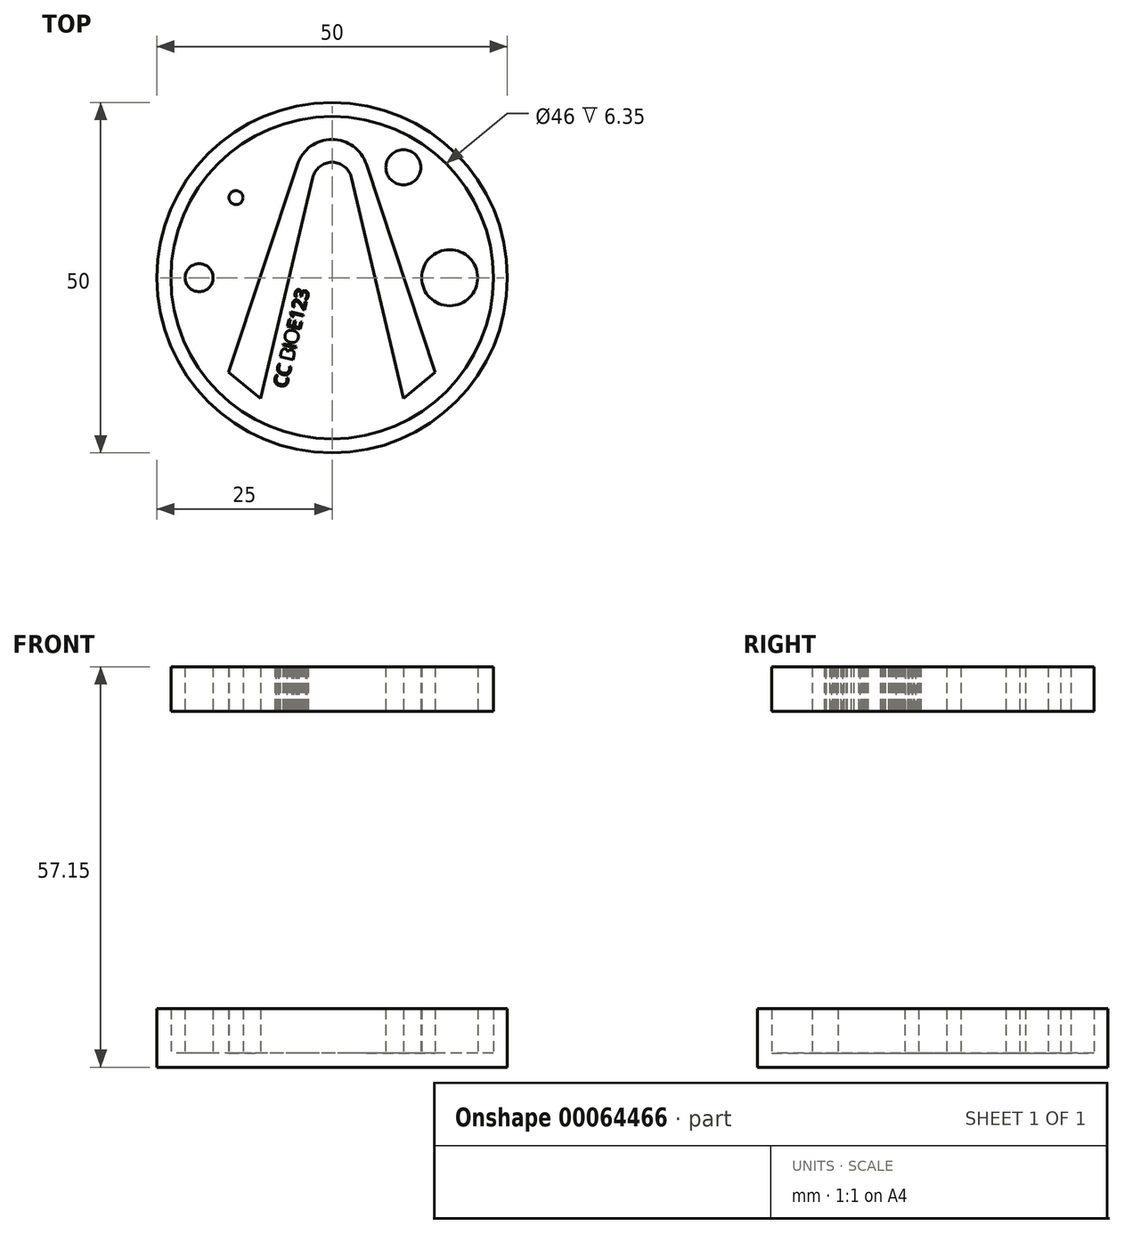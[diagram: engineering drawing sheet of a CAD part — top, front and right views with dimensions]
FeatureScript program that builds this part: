
annotation { "Feature Type Name" : "Feature", "Feature Type Description" : "" }
export const myFeature = defineFeature(function(context is Context, id is Id, definition is map)
    precondition{}
    {
        {
            var Q0;
            Q0=qCreatedBy(makeId("Top.planeOp"),FACE);
            var sketch = newSketch(context, id + "F0", { "sketchPlane" : qUnion([Q0])});
            skCircle(sketch, "E0", {"center": v(0, 0) * mm, "radius": 25 * mm});
            skCircle(sketch, "E1", {"center": v(0, 0) * mm, "radius": 23 * mm});
            skSolve(sketch);
        }
        {
            var Q0;
            Q0=makeQuery(id+"F0.imprint","IMPRINT",FACE,{"disambiguationData":[TD([[makeQuery(id+"F0.imprint","IMPRINT",EDGE,{"derivedFrom":sQuery(id+"F0.wireOp",EDGE,"E1")}),1.0]])]});
            extrude(context, id + "F1", {"entities" : qUnion([Q0]), "depth" : 2 * mm});
        }
        {
            var Q0;
            Q0=qCreatedBy(makeId("Top.planeOp"),FACE);
            cPlane(context, id + "F2", {"entities" : qUnion([Q0]), "cplaneType" : CPlaneType.OFFSET, "offset" : 50.8 * mm, "width" : 152.4 * mm, "height" : 152.4 * mm});
        }
        {
            var Q0;
            Q0=makeQuery(id+"F1.opExtrude","CAP_FACE",FACE,{"disambiguationData":[OSD([sQuery(id+"F0.wireOp",EDGE,"E1")])],"isStart":false});
            var sketch = newSketch(context, id + "F3", { "sketchPlane" : qUnion([Q0])});
            skArc(sketch, "E2", {"start": v(4.89, 16.16) * mm, "mid": v(-0.03, 19.72) * mm, "end": v(-4.95, 16.16) * mm});
            skArc(sketch, "E3", {"start": v(2.76, 14.29) * mm, "mid": v(0, 16.47) * mm, "end": v(-2.77, 14.29) * mm});
            skCircle(sketch, "E4", {"center": v(-18.97, 0) * mm, "radius": 2 * mm});
            skCircle(sketch, "E5", {"center": v(16.76, 0) * mm, "radius": 4 * mm});
            skCircle(sketch, "E6", {"center": v(-13.72, 11.43) * mm, "radius": 1 * mm});
            skCircle(sketch, "E7", {"center": v(10.16, 15.75) * mm, "radius": 2.5 * mm});
            skLineSegment(sketch, "E8", {"start": v(-4.95, 16.16) * mm, "end": v(-14.76, -13.5) * mm});
            skLineSegment(sketch, "E9", {"start": v(-2.77, 14.29) * mm, "end": v(-10.18, -17.21) * mm});
            skLineSegment(sketch, "E10", {"start": v(-14.76, -13.5) * mm, "end": v(-10.18, -17.21) * mm});
            skLineSegment(sketch, "E11", {"start": v(4.89, 16.16) * mm, "end": v(14.7, -13.5) * mm});
            skLineSegment(sketch, "E12", {"start": v(14.7, -13.5) * mm, "end": v(10.17, -17.21) * mm});
            skLineSegment(sketch, "E13", {"start": v(10.17, -17.21) * mm, "end": v(2.76, 14.29) * mm});
            skSolve(sketch);
        }
        {
            var Q0;
            Q0 = qSketchRegion(id + "F3", true);
            var Q1;
            {var subQ4=sQuery(id+"F3.wireOp",EDGE,"ofZBf3Q4-DUSz-Qi9E-emvZ-fDbDxGkiFMUY");Q1=makeQuery(id+"F3.imprint","IMPRINT",FACE,{"disambiguationData":[TD([[makeQuery(id+"F3.imprint","IMPRINT",EDGE,{"derivedFrom":subQ4}),-1.0]])]});}
            extrude(context, id + "F4", {"entities" : qUnion([Q0, Q1]), "operationType" : NewBodyOperationType.ADD, "depth" : 6.35 * mm});
        }
        {
            var Q0;
            Q0=makeQuery(id+"F0.imprint","IMPRINT",FACE,{"disambiguationData":[TD([[makeQuery(id+"F0.imprint","IMPRINT",EDGE,{"derivedFrom":sQuery(id+"F0.wireOp",EDGE,"E0")}),1.0]])]});
            extrude(context, id + "F5", {"entities" : qUnion([Q0]), "operationType" : NewBodyOperationType.ADD, "depth" : 8.35 * mm});
        }
        {
            var Q0;
            Q0=qCreatedBy(id+"F2.planeOp",FACE);
            var sketch = newSketch(context, id + "F6", { "sketchPlane" : qUnion([Q0])});
            skCircle(sketch, "E14", {"center": v(0, 0) * mm, "radius": 23 * mm});
            skArc(sketch, "E15", {"start": v(4.89, 16.16) * mm, "mid": v(-0.03, 19.72) * mm, "end": v(-4.95, 16.16) * mm});
            skArc(sketch, "E16", {"start": v(2.76, 14.29) * mm, "mid": v(0, 16.47) * mm, "end": v(-2.77, 14.29) * mm});
            skCircle(sketch, "E17", {"center": v(-18.97, 0) * mm, "radius": 2 * mm});
            skCircle(sketch, "E18", {"center": v(-13.72, 11.43) * mm, "radius": 1 * mm});
            skCircle(sketch, "E19", {"center": v(10.16, 15.75) * mm, "radius": 2.5 * mm});
            skCircle(sketch, "E20", {"center": v(16.76, 0) * mm, "radius": 4 * mm});
            skLineSegment(sketch, "E21", {"start": v(-2.77, 14.29) * mm, "end": v(-10.19, -17.21) * mm});
            skLineSegment(sketch, "E22", {"start": v(-4.95, 16.16) * mm, "end": v(-14.76, -13.5) * mm});
            skLineSegment(sketch, "E23", {"start": v(-14.76, -13.5) * mm, "end": v(-10.19, -17.21) * mm});
            skLineSegment(sketch, "E24", {"start": v(4.89, 16.16) * mm, "end": v(14.7, -13.5) * mm});
            skLineSegment(sketch, "E25", {"start": v(14.7, -13.5) * mm, "end": v(10.18, -17.21) * mm});
            skLineSegment(sketch, "E26", {"start": v(2.76, 14.29) * mm, "end": v(10.18, -17.21) * mm});
            skPoint(sketch, "E27", {"position": v(0, 19.72) * mm});
            skPoint(sketch, "E27.positionSnap0", {"position": v(-0.03, 19.72) * mm});
            skPoint(sketch, "E28", {"position": v(-0.03, 16.47) * mm});
            skText(sketch, "E29", { "text": "CC BIOE123", "fontName": "OpenSans-Regular.ttf"});
            const initialGuessF6  = {"E29": [-0.00656, -0.0158, 0.2292, 0.97338, 0.00188]};
            skSetInitialGuess(sketch, initialGuessF6);
            skSolve(sketch);
        }
        {
            var Q0;
            Q0 = qSketchRegion(id + "F6", true);
            extrude(context, id + "F7", {"entities" : qUnion([Q0]), "depth" : 6.35 * mm});
        }
        {
            var Q0;
            Q0=makeQuery(id+"F7.opExtrude","CAP_FACE",FACE,{"disambiguationData":[OSD([sQuery(id+"F6.wireOp",EDGE,"E14"),sQuery(id+"F6.wireOp",EDGE,"E15"),sQuery(id+"F6.wireOp",EDGE,"E16"),sQuery(id+"F6.wireOp",EDGE,"E17"),sQuery(id+"F6.wireOp",EDGE,"E18"),sQuery(id+"F6.wireOp",EDGE,"E19"),sQuery(id+"F6.wireOp",EDGE,"E20"),sQuery(id+"F6.wireOp",EDGE,"E21"),sQuery(id+"F6.wireOp",EDGE,"E22"),sQuery(id+"F6.wireOp",EDGE,"E23"),sQuery(id+"F6.wireOp",EDGE,"E24"),sQuery(id+"F6.wireOp",EDGE,"E25"),sQuery(id+"F6.wireOp",EDGE,"E26")])],"isStart":false});
            cPlane(context, id + "F8", {"entities" : qUnion([Q0]), "cplaneType" : CPlaneType.OFFSET, "offset" : 0 * mm, "width" : 150 * mm, "height" : 150 * mm});
        }
    });
